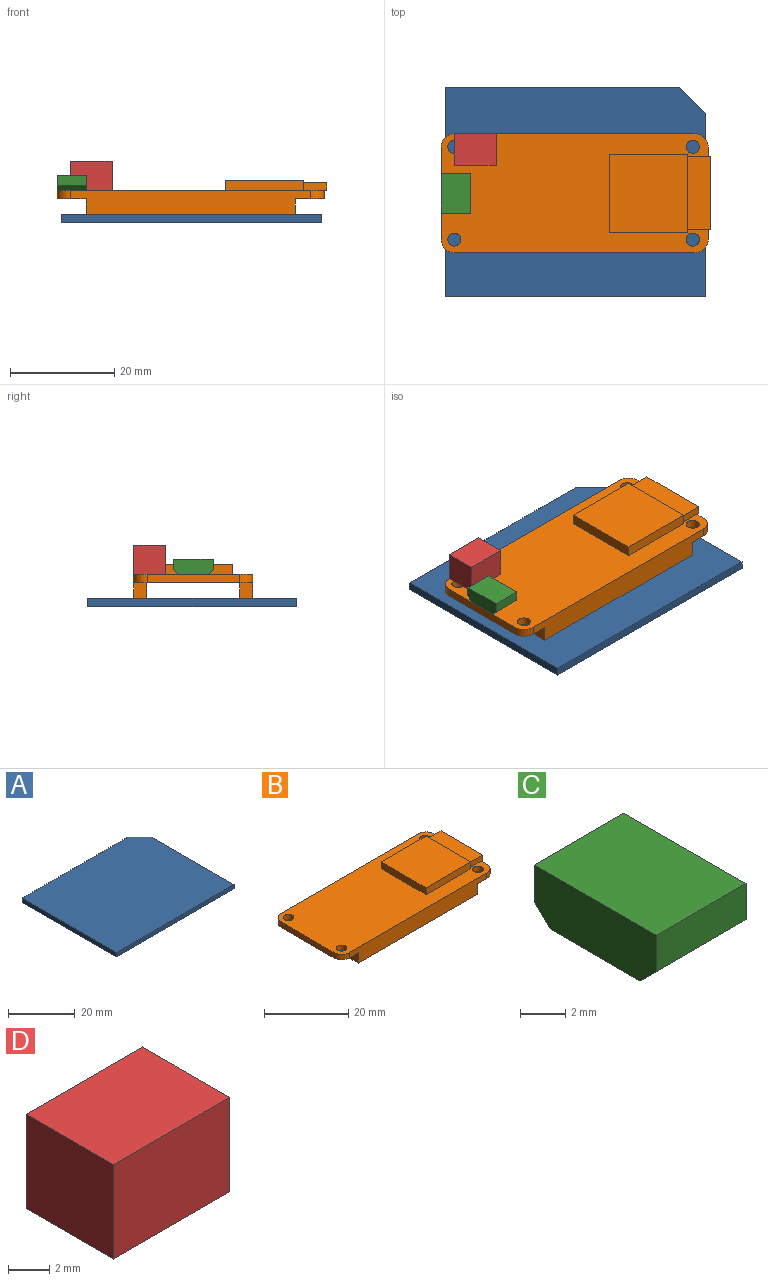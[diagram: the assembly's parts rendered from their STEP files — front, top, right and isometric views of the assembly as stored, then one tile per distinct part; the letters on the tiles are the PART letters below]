
ASSEMBLY  parts=4 mates=3
PART A: 7 faces, bbox 50x40x1.6 mm
  f0: plane 35x1.6mm, normal (1,0,0), area 56mm2, adj f3,f4,f5,f6
  f1: plane 45x1.6mm, normal (0,1,0), area 72mm2, adj f2,f4,f5,f6
  f2: plane 40x1.6mm, normal (-1,0,0), area 64mm2, adj f1,f3,f4,f5
  f3: plane 50x1.6mm, normal (0,-1,0), area 80mm2, adj f0,f2,f4,f5
  f4: plane 50x40mm, normal (0,0,-1), area 1987.5mm2, adj f0,f1,f2,f3,f6
  f5: plane 50x40mm, normal (0,0,1), area 1987.5mm2, adj f0,f1,f2,f3,f6
  f6: plane 5x5mm, normal (0.71,0.71,0), area 11.3mm2, adj f0,f1,f4,f5
PART B: 32 faces, bbox 51.7x22.8x6.6 mm
  f0: plane 15x2mm, normal (1,0,0), area 9mm2, adj f1,f15,f17,f18,f19,f20,f21
  f1: plane 51.2x22.8mm, normal (0,0,1), area 861.2mm2, adj f0,f2,f4,f5,f6,f7,f8,f9
  f2: cylinder r=2.54mm len=2.54mm, axis (0,0,-1), area 6.4mm2, adj f1,f3,f4,f14
  f3: plane 51.2x22.8mm, normal (0,0,-1), area 942.2mm2, adj f2,f4,f5,f6,f7,f8,f9,f10
  f4: plane 17.72x1.6mm, normal (1,0,0), area 28.4mm2, adj f1,f2,f3,f5,f22
  f5: cylinder r=2.54mm len=2.54mm, axis (0,0,-1), area 6.4mm2, adj f1,f3,f4,f13
  f6: cylinder r=2.54mm len=2.54mm, axis (0,0,-1), area 6.4mm2, adj f1,f3,f7,f14
  f7: plane 17.72x1.6mm, normal (-1,0,0), area 28.4mm2, adj f1,f3,f6,f8
  f8: cylinder r=2.54mm len=2.54mm, axis (0,0,-1), area 6.4mm2, adj f1,f3,f7,f13
  f9: cylinder r=1.25mm len=2.5mm, axis (0,0,-1), area 12.6mm2, adj f1,f3
  f10: cylinder r=1.25mm len=2.5mm, axis (0,0,-1), area 12.6mm2, adj f1,f3
  f11: cylinder r=1.25mm len=2.5mm, axis (0,0,-1), area 12.6mm2, adj f1,f3
  f12: cylinder r=1.25mm len=2.5mm, axis (0,0,-1), area 12.6mm2, adj f1,f3
  f13: plane 46.12x4.6mm, normal (0,-1,0), area 193.8mm2, adj f1,f3,f5,f8,f24,f25,f27
  f14: plane 46.12x4.6mm, normal (0,1,0), area 193.8mm2, adj f1,f2,f3,f6,f28,f30,f31
  f15: plane 15x2mm, normal (0,1,0), area 30mm2, adj f0,f1,f16,f18
  f16: plane 15x2mm, normal (-1,0,0), area 30mm2, adj f1,f15,f17,f18
  f17: plane 15x2mm, normal (0,-1,0), area 30mm2, adj f0,f1,f16,f18
  f18: plane 15x15mm, normal (0,0,1), area 225mm2, adj f0,f15,f16,f17
  f19: plane 4.5x1.5mm, normal (0,1,0), area 6.8mm2, adj f0,f1,f20,f22,f23
  f20: plane 14x4.5mm, normal (0,0,1), area 63mm2, adj f0,f19,f21,f23
  f21: plane 4.5x1.5mm, normal (0,-1,0), area 6.8mm2, adj f0,f1,f20,f22,f23
  f22: plane 14x0.5mm, normal (0,0,-1), area 7mm2, adj f4,f19,f21,f23
  f23: plane 14x1.5mm, normal (1,0,0), area 21mm2, adj f19,f20,f21,f22
  f24: plane 3x2.5mm, normal (1,0,0), area 7.5mm2, adj f3,f13,f26,f27
  f25: plane 3x2.5mm, normal (-1,0,0), area 7.5mm2, adj f3,f13,f26,f27
  f26: plane 40x3mm, normal (0,1,0), area 120mm2, adj f3,f24,f25,f27
  f27: plane 40x2.5mm, normal (0,0,-1), area 100mm2, adj f13,f24,f25,f26
  f28: plane 3x2.5mm, normal (1,0,0), area 7.5mm2, adj f3,f14,f29,f31
  f29: plane 40x3mm, normal (0,-1,0), area 120mm2, adj f3,f28,f30,f31
  f30: plane 3x2.5mm, normal (-1,0,0), area 7.5mm2, adj f3,f14,f29,f31
  f31: plane 40x2.5mm, normal (0,0,-1), area 100mm2, adj f14,f28,f29,f30
PART C: 8 faces, bbox 5.6x7.6x3 mm
  f0: plane 5.6x1mm, normal (0,-0.71,-0.71), area 7.9mm2, adj f1,f2,f5,f7
  f1: plane 5.6x1.95mm, normal (0,-1,0), area 10.9mm2, adj f0,f2,f5,f6
  f2: plane 7.6x2.95mm, normal (1,0,0), area 21.4mm2, adj f0,f1,f3,f4,f6,f7
  f3: plane 5.6x1mm, normal (0,0.71,-0.71), area 7.9mm2, adj f2,f4,f5,f7
  f4: plane 5.6x1.95mm, normal (0,1,0), area 10.9mm2, adj f2,f3,f5,f6
  f5: plane 7.6x2.95mm, normal (-1,0,0), area 21.4mm2, adj f0,f1,f3,f4,f6,f7
  f6: plane 7.6x5.6mm, normal (0,0,1), area 42.6mm2, adj f1,f2,f4,f5
  f7: plane 5.6x5.6mm, normal (0,0,-1), area 31.4mm2, adj f0,f2,f3,f5
PART D: 6 faces, bbox 8x6x5.6 mm
  f0: plane 6x5.6mm, normal (-1,0,0), area 33.6mm2, adj f1,f3,f4,f5
  f1: plane 8x5.6mm, normal (0,1,0), area 44.8mm2, adj f0,f2,f4,f5
  f2: plane 6x5.6mm, normal (1,0,0), area 33.6mm2, adj f1,f3,f4,f5
  f3: plane 8x5.6mm, normal (0,-1,0), area 44.8mm2, adj f0,f2,f4,f5
  f4: plane 8x6mm, normal (0,0,1), area 48mm2, adj f0,f1,f2,f3
  f5: plane 8x6mm, normal (0,0,-1), area 48mm2, adj f0,f1,f2,f3
PLACE A at identity fixed
PLACE B t=(-1.55,-0.25,4.6)mm
PLACE C t=(-1.55,-0.28,4.6)mm
PLACE D t=(-5.67,-0.25,4.6)mm
MATE fastened C.f7 <-> B.f1  axis (0,0,-1) through (-1.55,11.15,4.6)mm
MATE fastened A.f5 <-> B.f31  axis (0,0,1) through (24.05,11.3,0)mm
MATE fastened B.f1 <-> D.f5  axis (0,0,1) through (0.99,22.55,4.6)mm
